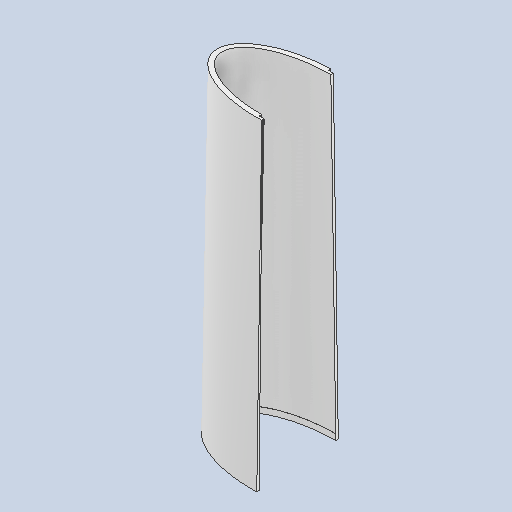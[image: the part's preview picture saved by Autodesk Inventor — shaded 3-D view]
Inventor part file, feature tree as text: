
AUTODESK INVENTOR PART (.ipt)
format: ipt  version: 2022 (Build 260153000, 153)  size: 212,992 bytes
history: native  units: in
note: dims shown in document units (in); Inventor stores cm internally (conversion verified against a paired STEP export)
features: sketch x5, plane x2, extrude x2, loft x1, fillet x1, hole x1
ambient origin geometry x8: Origin, YZ Plane, XZ Plane, XY Plane, X Axis, Y Axis, Z Axis, Center Point
bodies: Body1 (feature_tree)
feature tree (12):
  sketch  "Sketch18"  dims[d92=6.3583in d100=0.0in d101=90.0deg]
  plane  "Work Plane4"
  loft  "Loft4"
  plane  "Work Plane5"
  extrude  "Extrusion8"  Depth=0.2362in TaperAngle=0.0deg
  fillet  "Fillet2"  Radius=0.0787in
  hole  "Hole3"  [1 undecoded]
  extrude  "Extrusion9"  Depth=0.0344in
  sketch  "Sketch19"  dims[d102=0.0in d103=90.0deg d110=0.2362in d111=0.0in d112=0.0787in]
  sketch  "Sketch21"  dims[d113=0.1969in]
  sketch  "Sketch22"  dims[d114=0.1181in d115=0.2362in d116=0.1575in d117=0.0787in d118=90.0deg d119=0.3543in d120=0.0in d121=0.1181in d122=0.0in]
  sketch  "Sketch23"  dims[d108=0.0197in d109=0.0344in]
note: 1 required parameter value undecoded (feature->parameter linkage not recoverable at this tier; creation-order binding heuristic only, values carry confidence <= 0.55)
